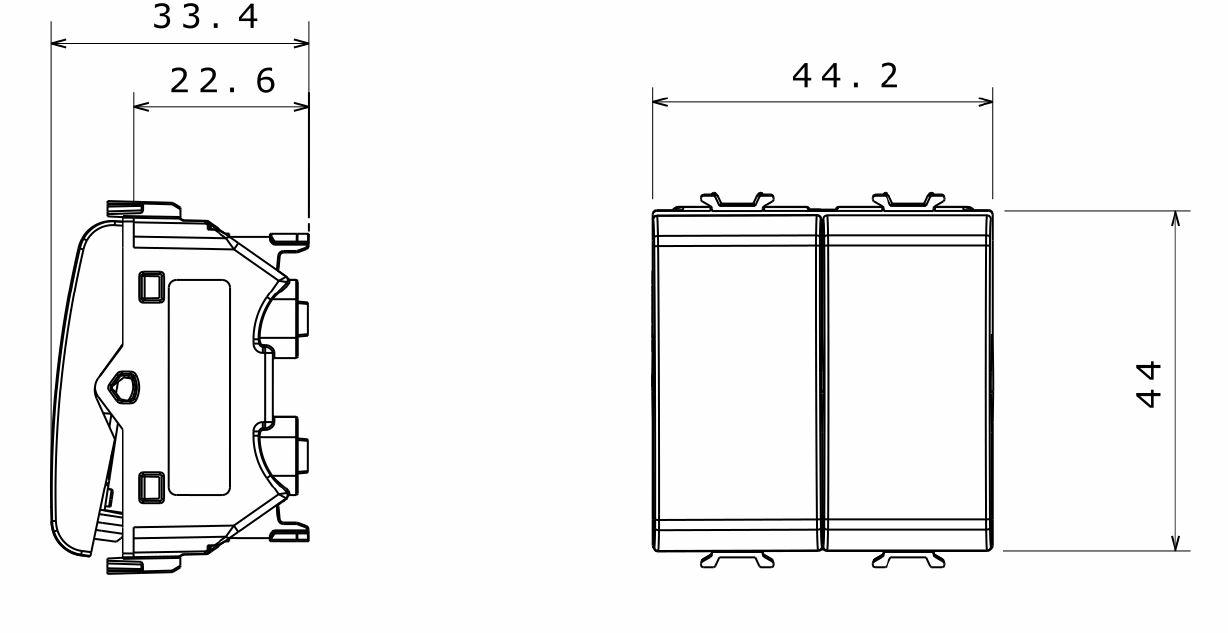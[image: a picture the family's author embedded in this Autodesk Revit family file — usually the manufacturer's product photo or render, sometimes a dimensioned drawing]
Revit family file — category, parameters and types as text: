
# Revit family: Domotics-DomesticRanges-GEWISS-CHORUS_COMMAND-PUSH-BUTTON_ELECTRONIC_2M
name_source: partatom
category: Apparecchi elettrici
revit_build: Autodesk Revit 2016 (Build: 20161004_0715(x64)
units: mm (PartAtom-declared; Revit-internal decimal feet)

## family parameters
Condiviso = Sì
Host = Superficie
Mantenere orientamento annotazione = Sì
Punto di calcolo locali = Sì
Quota connettore circolare = Usa diametro
Taglio con vuoti quando caricato = Sì
Tipo di parte = Normale

## types (6) — shared parameters
17 = No
18 = Sì
Catalogue = DOMOTICS
Catalogue Range = CHORUS - DOMESTIC RANGE
Description. = Electronic push-button
Electrocod = 0144
IDF = 568fd9f2-3731-4a5a-933f-4a1efe494eb3
IDT = 4ca41d65-6c8f-45c9-b2d9-76c5349e6005
Immagine tipo = GW14918.jpg
Inputs = BUS
No. Chorus modules = 2
No. Chorus modules: = 2
Produttore = GEWISS S.p.A.
Prospetto di default = 1219 mm
SEO = Push button
Supply voltage = Backlit
Technical sheet = https://www.gewiss.com
Tipo_ = CHORUS PULSANTI ELETTRONICI 2M_GENERICO : GW14918 Pulsante elettronico 2M segnalazione luminosa titanio
Type of use = Bus contacts interfaces
Type: = Backlit
URL = https://www.gewiss.com
Version file RFA = 19.0

## per-type parameters (varying)
| type | Button key | Colour | Descrizione | EAN code | Modello | Type | Type of use: |
| GW12917 - Electronic push-button 2M backlit black | With diffuser | Black | ELECTRONIC PUSH-BUTTON 2M BACKLIT BL | 8011564816459 | GW12917 | Backlit |  |
| GW14917 - Electronic push-button 2M backlit titanium | With diffuser | Titanium | ELECTRONIC PUSH-BUTTON 2M BACKLIT TI. | 8011564816480 | GW14917 | Backlit |  |
| GW10917 - Electronic push-button 2M backlit white | With diffuser | White | ELECTRONIC PUSH-BUTTON 2M BACKLIT WH | 8011564816428 | GW10917 | Backlit | Bus contacts interfaces |
| GW10918 - Electronic push-button 2M indicator white | With replaceable neutral lens | White | ELECTRONIC PUSH-BUTTON 2M INDICATOR WH | 8011564816435 | GW10918 | Indicator | Bus contacts interfaces |
| GW12918 - Electronic push-button 2M indicator black | With replaceable neutral lens | Black | ELECTRONIC PUSH-BUTTON 2M INDICATOR BL. | 8011564816466 | GW12918 | Indicator |  |
| GW14918 - Electronic push-button 2M indicator titanium | With replaceable neutral lens | Titanium | ELECTRONIC PUSH-BUTTON 2M INDICATOR TI. | 8011564816497 | GW14918 | Indicator |  |

## geometry (parser evidence)
native form markers: Sweep x1
no freeform markers — native parametric forms only
